# Revit family: PRMD
name_source: partatom
category: Lighting Fixtures
units: mm (PartAtom-declared; Revit-internal decimal feet)

## family parameters
Cut with Voids When Loaded = No
Host = Face
Light Source = No
OmniClass Number = 23.80.70.14
OmniClass Title = Luminaries for External Lighting
Part Type = Normal
Room Calculation Point = No
Round Connector Dimension = Use Diameter
Shared = No

## types (13) — shared parameters
Apparent Load = 0 VA
Default Elevation = 48.000"
Description = PROMENADE – PRMD
Glass = Glass-Frosted
Lamp = ED-17 & ED-18
Load Classification = Lighting
Manufacturer = Architectural Area Lighting
Model = PRMD
URL = https://www.currentlighting.com
Wattage Comments = 50-250W

## per-type parameters (varying)
| type | Finish |
| PRMD - AWT | Aluminum-Artic White |
| PRMD - BLK | Aluminum-Black |
| PRMD - MTB | Aluminum-Matte Black |
| PRMD - DGN | Aluminum-Dark Green |
| PRMD - DBZ | Aluminum-Dark Bronze |
| PRMD - WRZ | Aluminum-Weathered Bronze |
| PRMD - BRM | Aluminum-Metalic Bronze |
| PRMD - VBL | Aluminum-Verde Blue |
| PRMD - CRT | Aluminum-Corten |
| PRMD - MAL | Aluminum-Matte |
| PRMD - MDG | Aluminum-Medium Grey |
| PRMD - ATG | Aluminum-Antique Green |
| PRMD - LGY | Aluminum-Light Grey |

## geometry (parser evidence)
native form markers: Blend x36, Sweep x6
no freeform markers — native parametric forms only
